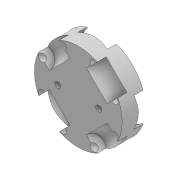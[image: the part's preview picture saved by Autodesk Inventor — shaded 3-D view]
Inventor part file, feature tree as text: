
AUTODESK INVENTOR PART (.ipt)
format: ipt  version: 2017 (Build 210142000, 142)  size: 203,264 bytes
history: native  units: mm
features: sketch x4, revolve x2, pattern_circular x2, extrude x1, hole x1
ambient origin geometry x8: Origin, YZ Plane, XZ Plane, XY Plane, X Axis, Y Axis, Z Axis, Center Point
bodies: Solid1 (feature_tree)
feature tree (10):
  extrude  "Extrusion1"  Depth=16.0mm TaperAngle=0.0deg
  revolve  "Revolution1"  [1 undecoded]
  pattern_circular  "Circular Pattern2"  [2 undecoded]
  revolve  "Revolution2"  [1 undecoded]
  pattern_circular  "Circular Pattern3"  Angle=90.0deg  [1 undecoded]
  hole  "Hole1"  [1 undecoded]
  sketch  "Sketch1"  dims[d0=60.0mm d1=16.0mm d2=0.0mm]
  sketch  "Sketch2"  dims[d3=14.0mm d4=25.0mm]
  sketch  "Sketch3"  dims[d5=6.0mm]
  sketch  "Sketch4"  dims[d6=5.0mm d7=5.0mm d8=20.0mm d9=90.0deg d13=40.0mm d14=360.0deg d16=45.0deg d17=25.0mm d18=14.0mm d19=20.0mm d20=5.0mm d21=5.0mm d22=90.0deg d23=40.0mm d24=360.0deg d26=14.0mm d27=14.0mm d28=4.0mm d29=6.0mm d30=4.0mm d31=2.0mm d32=90.0deg d33=8.0mm d34=20.594885mm]
note: 6 required parameter values undecoded (feature->parameter linkage not recoverable at this tier; creation-order binding heuristic only, values carry confidence <= 0.55)